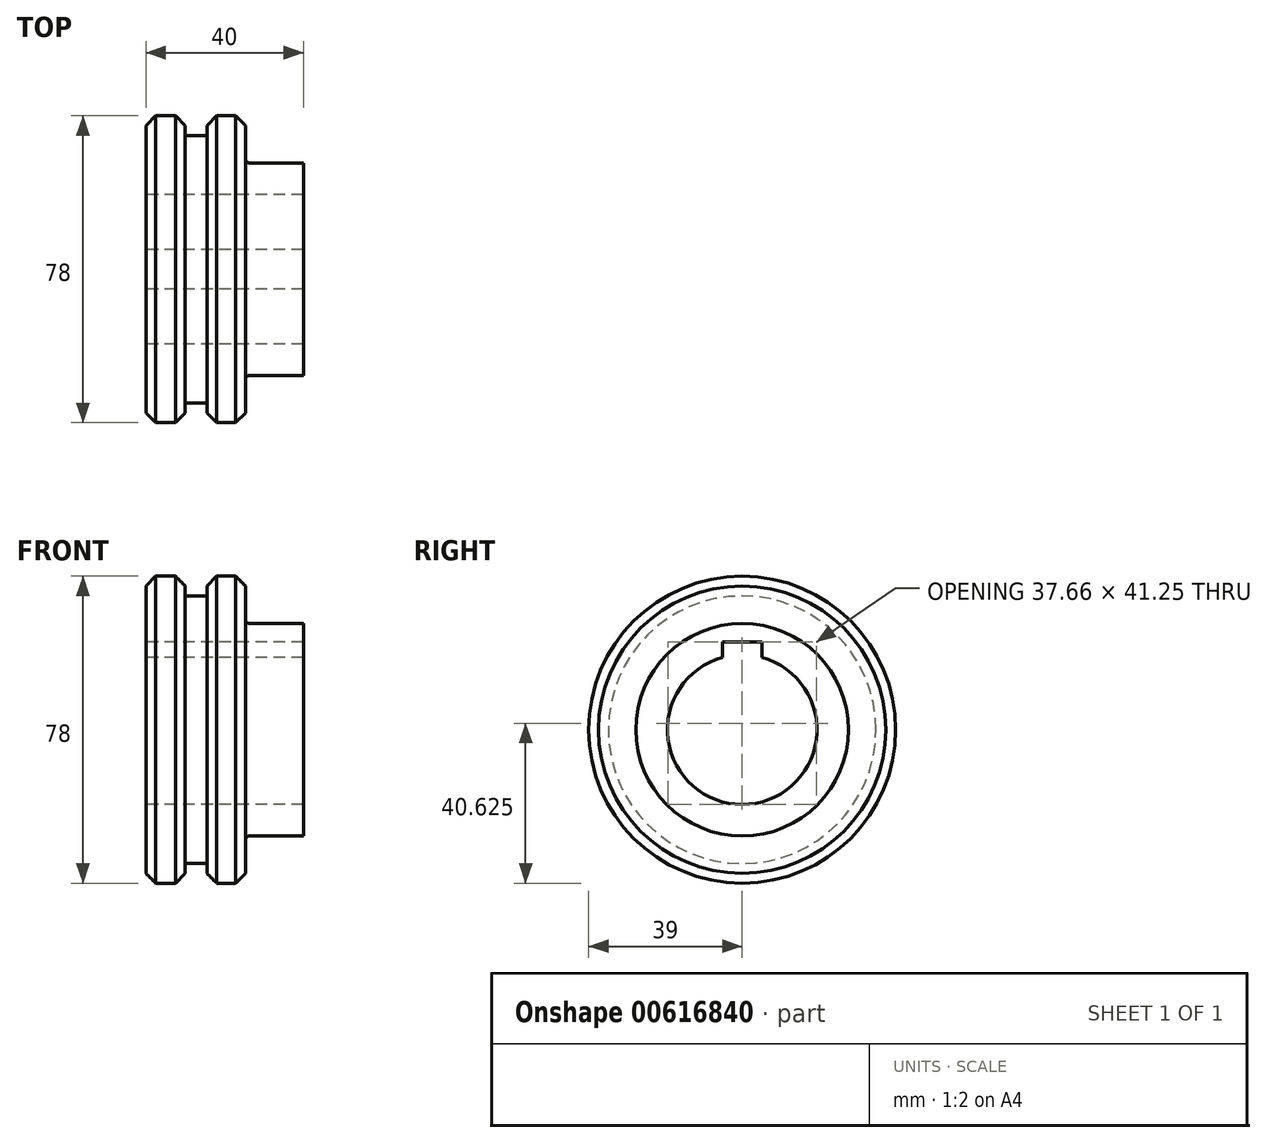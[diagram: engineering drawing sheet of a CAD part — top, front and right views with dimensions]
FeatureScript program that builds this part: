
annotation { "Feature Type Name" : "Feature", "Feature Type Description" : "" }
export const myFeature = defineFeature(function(context is Context, id is Id, definition is map)
    precondition{}
    {
        {
            var Q0;
            Q0=qCreatedBy(makeId("Front.planeOp"),FACE);
            var sketch = newSketch(context, id + "F0", { "sketchPlane" : qUnion([Q0])});
            skLineSegment(sketch, "E0", {"start": v(0, 39) * mm, "end": v(0, 19) * mm});
            skLineSegment(sketch, "E1", {"start": v(0, 19) * mm, "end": v(40, 19) * mm});
            skLineSegment(sketch, "E2", {"start": v(40, 19) * mm, "end": v(40, 27) * mm});
            skLineSegment(sketch, "E3", {"start": v(40, 27) * mm, "end": v(25.3, 27) * mm});
            skLineSegment(sketch, "E4", {"start": v(25.3, 27) * mm, "end": v(25.3, 39) * mm});
            skLineSegment(sketch, "E5", {"start": v(25.3, 39) * mm, "end": v(15.5, 39) * mm});
            skLineSegment(sketch, "E6", {"start": v(15.5, 39) * mm, "end": v(15.5, 34) * mm});
            skLineSegment(sketch, "E7", {"start": v(15.5, 34) * mm, "end": v(10, 34) * mm});
            skLineSegment(sketch, "E8", {"start": v(10, 34) * mm, "end": v(10, 39) * mm});
            skLineSegment(sketch, "E9", {"start": v(10, 39) * mm, "end": v(0, 39) * mm});
            skLineSegment(sketch, "E10", {"start": v(0, 0) * mm, "end": v(58.67, 0) * mm, "construction": true});
            skSolve(sketch);
        }
        {
            var Q0;
            Q0=makeQuery(id+"F0.imprint","IMPRINT",FACE,{"disambiguationData":[TD([[makeQuery(id+"F0.imprint","IMPRINT",EDGE,{"derivedFrom":sQuery(id+"F0.wireOp",EDGE,"E0")}),1.0]])]});
            var Q1;
            Q1=sQuery(id+"F0.wireOp",EDGE,"E10");
            revolve(context, id + "F1", {"surfaceOperationType" : NewSurfaceOperationType.NEW, "entities" : qUnion([Q0]), "axis" : qUnion([Q1]), "revolveType" : RevolveType.FULL});
        }
        {
            var Q0;
            Q0=makeQuery(id+"F1.opRevolve","SWEPT_EDGE",EDGE,{"disambiguationData":[OSD([sQuery(id+"F0.wireOp",EDGE,"E0"),sQuery(id+"F0.wireOp",EDGE,"E9")])]});
            var Q1;
            Q1=makeQuery(id+"F1.opRevolve","SWEPT_EDGE",EDGE,{"disambiguationData":[OSD([sQuery(id+"F0.wireOp",EDGE,"E8"),sQuery(id+"F0.wireOp",EDGE,"E9")])]});
            var Q2;
            Q2=makeQuery(id+"F1.opRevolve","SWEPT_EDGE",EDGE,{"disambiguationData":[OSD([sQuery(id+"F0.wireOp",EDGE,"E5"),sQuery(id+"F0.wireOp",EDGE,"E6")])]});
            var Q3;
            Q3=makeQuery(id+"F1.opRevolve","SWEPT_EDGE",EDGE,{"disambiguationData":[OSD([sQuery(id+"F0.wireOp",EDGE,"E4"),sQuery(id+"F0.wireOp",EDGE,"E5")])]});
            chamfer(context, id + "F2", {"entities" : qUnion([Q0, Q1, Q2, Q3]), "width" : 2.5 * mm, "tangentPropagation" : true});
        }
        {
            var Q0;
            Q0=qCreatedBy(makeId("Right.planeOp"),FACE);
            var sketch = newSketch(context, id + "F3", { "sketchPlane" : qUnion([Q0])});
            skLineSegment(sketch, "E11.bottom", {"start": v(5, 22.25) * mm, "end": v(-5, 22.25) * mm});
            skLineSegment(sketch, "E11.top", {"start": v(5, 13.25) * mm, "end": v(-5, 13.25) * mm});
            skLineSegment(sketch, "E11.left", {"start": v(5, 22.25) * mm, "end": v(5, 13.25) * mm});
            skLineSegment(sketch, "E11.right", {"start": v(-5, 22.25) * mm, "end": v(-5, 13.25) * mm});
            skPoint(sketch, "E11.middle", {"position": v(0, 17.75) * mm});
            skCircle(sketch, "E12.0", {"center": v(0, 0) * mm, "radius": 19 * mm, "construction": true});
            skSolve(sketch);
        }
        {
            var Q0;
            Q0 = qSketchRegion(id + "F3", true);
            extrude(context, id + "F4", {"entities" : qUnion([Q0]), "operationType" : NewBodyOperationType.REMOVE, "endBound" : BoundingType.THROUGH_ALL, "depth" : 25 * mm, "offsetDistance" : 25 * mm});
        }
        {
            var Q0;
            Q0=makeQuery(id+"F1.opRevolve","SWEPT_EDGE",EDGE,{"disambiguationData":[OSD([sQuery(id+"F0.wireOp",EDGE,"E3"),sQuery(id+"F0.wireOp",EDGE,"E4")])]});
            fillet(context, id + "F5", {"entities" : qUnion([Q0]), "radius" : 1 * mm, "tangentPropagation" : true, "allowEdgeOverflow" : false});
        }
    });
